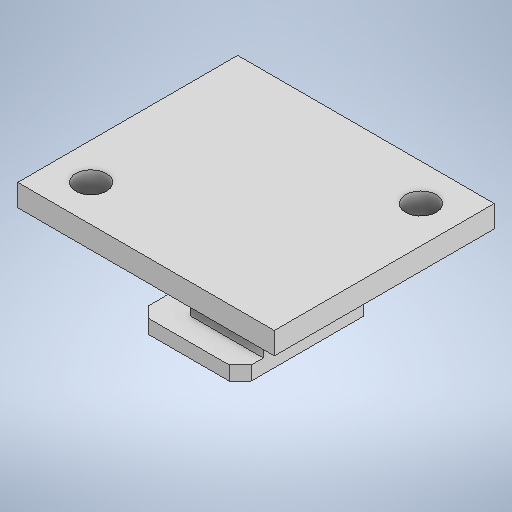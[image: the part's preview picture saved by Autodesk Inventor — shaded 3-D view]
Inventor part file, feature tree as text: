
AUTODESK INVENTOR PART (.ipt)
format: ipt  version: 2025.1 (Build 291241000, 241)  size: 247,296 bytes
history: native  units: mm
features: sketch x4, extrude x3, chamfer x1, hole x1
ambient origin geometry x8: Origin, YZ Plane, XZ Plane, XY Plane, X Axis, Y Axis, Z Axis, Center Point
bodies: Volumenkörper1 (feature_tree)
feature tree (9):
  extrude  "Extrusion1"  Depth=18.3mm
  chamfer  "Fasen1"  Distance=1.9mm
  extrude  "Extrusion2"  Depth=10.0mm
  extrude  "Extrusion3"  Depth=10.0mm TaperAngle=0.0deg
  hole  "Bohrung1"  [1 undecoded]
  sketch  "Skizze1"  dims[d0=14.0mm d1=18.3mm d2=1.9mm d3=0.0mm]
  sketch  "Skizze2"  dims[d4=1.5mm d5=2.0mm d6=45.0deg d7=10.0mm]
  sketch  "Skizze3"  dims[d8=12.0mm d9=10.0mm d10=0.0mm]
  sketch  "Skizze4"  dims[d11=35.0mm d12=30.0mm d13=3.0mm d14=0.0mm d15=25.0mm d16=20.0mm d17=4.2mm d18=6.0mm d19=4.0mm d20=2.0mm d21=90.0deg d22=8.0mm d23=20.594885mm]
note: 1 required parameter value undecoded (feature->parameter linkage not recoverable at this tier; creation-order binding heuristic only, values carry confidence <= 0.55)
